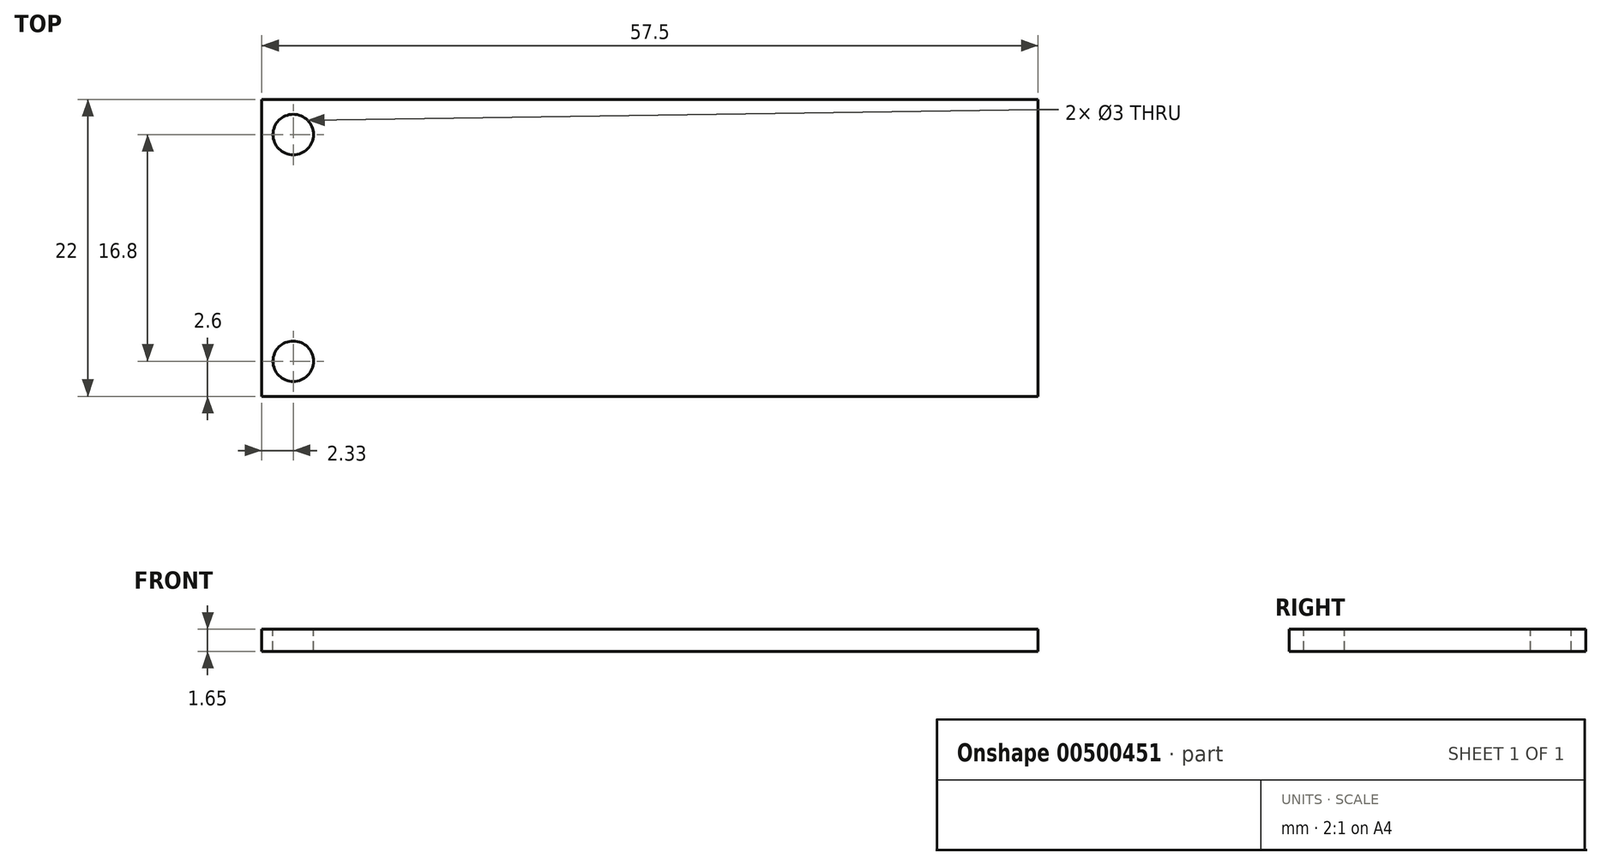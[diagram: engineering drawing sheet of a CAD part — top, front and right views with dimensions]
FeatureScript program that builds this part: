
annotation { "Feature Type Name" : "Feature", "Feature Type Description" : "" }
export const myFeature = defineFeature(function(context is Context, id is Id, definition is map)
    precondition{}
    {
        {
            var Q0;
            Q0=qCreatedBy(makeId("Top.planeOp"),FACE);
            var sketch = newSketch(context, id + "F0", { "sketchPlane" : qUnion([Q0])});
            skLineSegment(sketch, "E0.bottom", {"start": v(28.75, 11) * mm, "end": v(-28.75, 11) * mm});
            skLineSegment(sketch, "E0.top", {"start": v(28.75, -11) * mm, "end": v(-28.75, -11) * mm});
            skLineSegment(sketch, "E0.left", {"start": v(28.75, 11) * mm, "end": v(28.75, -11) * mm});
            skLineSegment(sketch, "E0.right", {"start": v(-28.75, 11) * mm, "end": v(-28.75, -11) * mm});
            skPoint(sketch, "E0.middle", {"position": v(0, 0) * mm});
            skSolve(sketch);
        }
        {
            var Q0;
            Q0 = qSketchRegion(id + "F0", true);
            extrude(context, id + "F1", {"entities" : qUnion([Q0]), "depth" : 1.65 * mm});
        }
        {
            var Q0;
            Q0=makeQuery(id+"F1.opExtrude","CAP_FACE",FACE,{"disambiguationData":[OSD([sQuery(id+"F0.wireOp",EDGE,"E0.bottom"),sQuery(id+"F0.wireOp",EDGE,"E0.top"),sQuery(id+"F0.wireOp",EDGE,"E0.left"),sQuery(id+"F0.wireOp",EDGE,"E0.right")])],"isStart":false});
            var sketch = newSketch(context, id + "F2", { "sketchPlane" : qUnion([Q0])});
            skLineSegment(sketch, "E1", {"start": v(-28.75, 0) * mm, "end": v(28.75, 0) * mm, "construction": true});
            skCircle(sketch, "E2", {"center": v(-26.42, -8.4) * mm, "radius": 1.5 * mm});
            skCircle(sketch, "E3.MirrorC", {"center": v(-26.42, 8.4) * mm, "radius": 1.5 * mm});
            skSolve(sketch);
        }
        {
            var Q0;
            Q0 = qSketchRegion(id + "F2", true);
            extrude(context, id + "F3", {"entities" : qUnion([Q0]), "operationType" : NewBodyOperationType.REMOVE, "endBound" : BoundingType.THROUGH_ALL, "oppositeDirection" : true, "depth" : 25.4 * mm});
        }
        {
            var Q0;
            Q0=makeQuery(id+"F1.opExtrude","CAP_FACE",FACE,{"disambiguationData":[OSD([sQuery(id+"F0.wireOp",EDGE,"E0.bottom"),sQuery(id+"F0.wireOp",EDGE,"E0.top"),sQuery(id+"F0.wireOp",EDGE,"E0.left"),sQuery(id+"F0.wireOp",EDGE,"E0.right")])],"isStart":false});
            var sketch = newSketch(context, id + "F4", { "sketchPlane" : qUnion([Q0])});
            skLineSegment(sketch, "E4", {"start": v(-28.75, 0) * mm, "end": v(28.75, 0) * mm, "construction": true});
            skLineSegment(sketch, "E5", {"start": v(0, 11) * mm, "end": v(0, -11) * mm, "construction": true});
            skSolve(sketch);
        }
    });
